# Revit family: Verano_V918_Purbeck_GM_R21
name_source: partatom
category: Generic Models
units: mm (PartAtom-declared; Revit-internal decimal feet)

## family parameters
Always vertical = Yes
Can host rebar = No
Cut with Voids When Loaded = No
Part Type = Normal
Room Calculation Point = No
Round Connector Dimension = Use Diameter
Shared = No
Work Plane-Based = No

## types (1)
- Verano_V918_Purbeck_GM_R21
    Default Elevation = 0 mm  [stored 0 ft]
    Gasket Material = <By Category>
    Manufacturer = Verano Systems
    Maximal Inclination Angle = 15.00°
    Maximal Overall Width = 14000 mm  [stored 45.9318 ft]
    Maximal Projection = 3000 mm  [stored 9.84252 ft]
    Minimal Inclination Angle = 5.00°
    Minimal Overall Width = 3000 mm  [stored 9.84252 ft]
    Minimal Projection = 2000 mm  [stored 6.56168 ft]
    Model = V918 Purbeck
    URL = www.verano.nl

note: [stored X ft] marks values corroborated as IEEE doubles in the binary element streams (Revit-internal decimal feet)

## geometry (parser evidence)
native form markers: Extrusion x2, Sweep x24
no freeform markers — native parametric forms only
